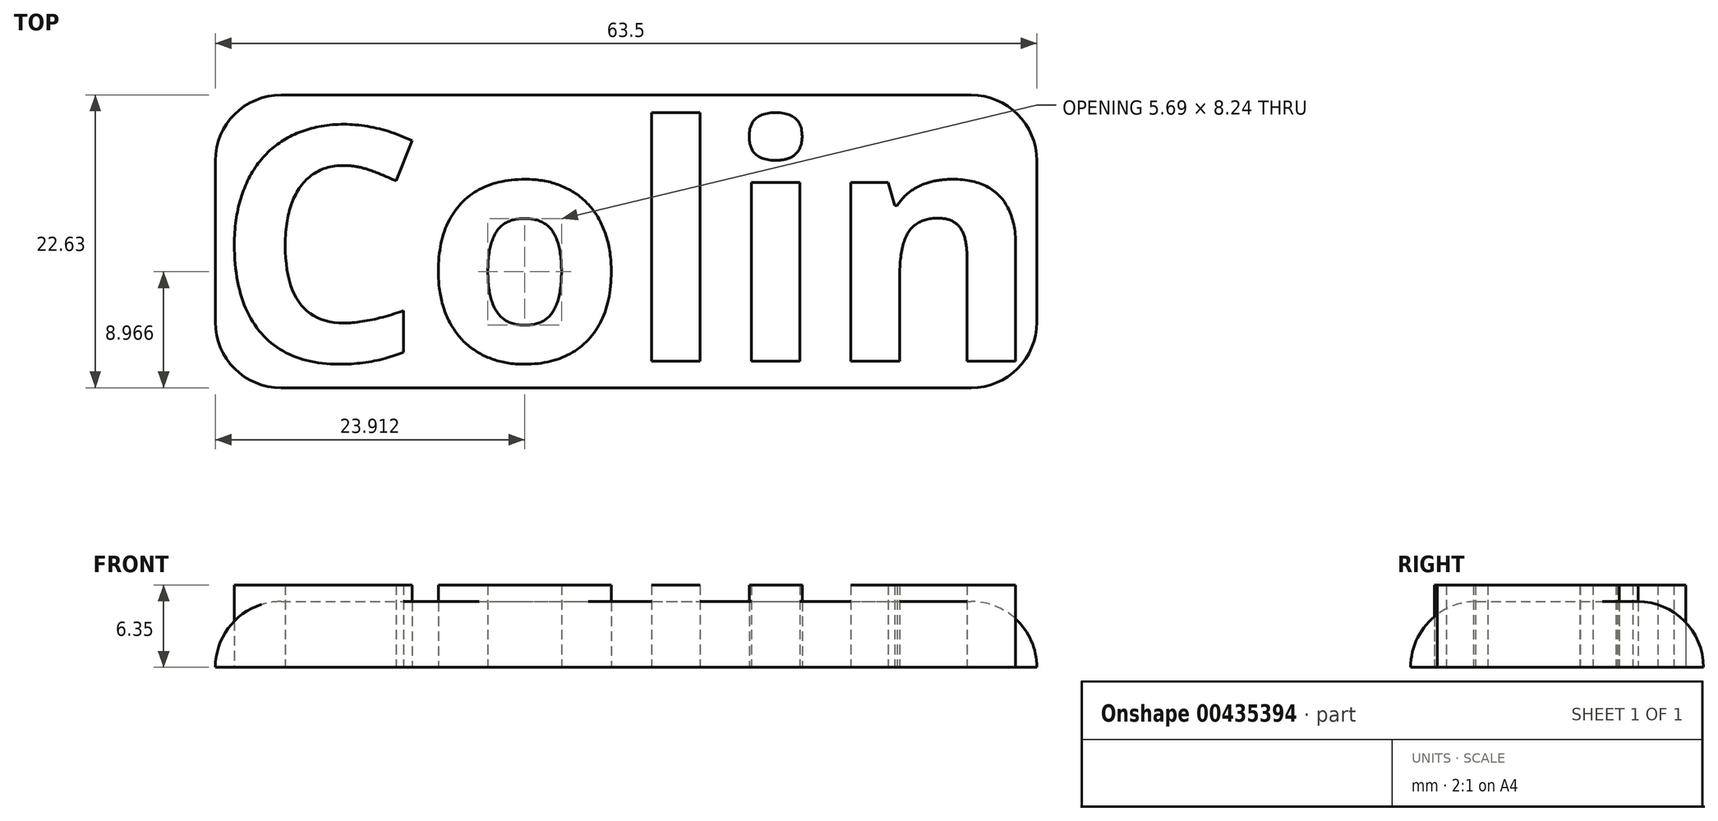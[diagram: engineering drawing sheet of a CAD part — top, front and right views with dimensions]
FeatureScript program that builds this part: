
annotation { "Feature Type Name" : "Feature", "Feature Type Description" : "" }
export const myFeature = defineFeature(function(context is Context, id is Id, definition is map)
    precondition{}
    {
        {
            var Q0;
            Q0=qCreatedBy(makeId("Top.planeOp"),FACE);
            var sketch = newSketch(context, id + "F0", { "sketchPlane" : qUnion([Q0])});
            skText(sketch, "E0", { "text": "Colin", "fontName": "OpenSans-Bold.ttf"});
            const initialGuessF0  = {"E0": [0, 0, 1, 0, 0.01819]};
            skSetInitialGuess(sketch, initialGuessF0);
            skSolve(sketch);
        }
        {
            var Q0;
            Q0=qCreatedBy(makeId("Top.planeOp"),FACE);
            var sketch = newSketch(context, id + "F1", { "sketchPlane" : qUnion([Q0])});
            skLineSegment(sketch, "E1.bottom", {"start": v(0, -2.07) * mm, "end": v(63.5, -2.07) * mm});
            skLineSegment(sketch, "E1.top", {"start": v(0, 20.56) * mm, "end": v(63.5, 20.56) * mm});
            skLineSegment(sketch, "E1.left", {"start": v(0, -2.07) * mm, "end": v(0, 20.56) * mm});
            skLineSegment(sketch, "E1.right", {"start": v(63.5, -2.07) * mm, "end": v(63.5, 20.56) * mm});
            skSolve(sketch);
        }
        {
            var Q0;
            Q0 = qSketchRegion(id + "F0", true);
            extrude(context, id + "F2", {"entities" : qUnion([Q0]), "depth" : 6.35 * mm});
        }
        {
            var Q0;
            Q0=makeQuery(id+"F1.imprint","IMPRINT",FACE,{"disambiguationData":[TD([[makeQuery(id+"F1.imprint","IMPRINT",EDGE,{"derivedFrom":sQuery(id+"F1.wireOp",EDGE,"E1.bottom")}),1.0]])]});
            extrude(context, id + "F3", {"entities" : qUnion([Q0]), "depth" : 5.08 * mm});
        }
        {
            var Q0;
            Q0=makeQuery(id+"F3.opExtrude","CAP_FACE",FACE,{"disambiguationData":[OSD([sQuery(id+"F1.wireOp",EDGE,"E1.bottom"),sQuery(id+"F1.wireOp",EDGE,"E1.top"),sQuery(id+"F1.wireOp",EDGE,"E1.left"),sQuery(id+"F1.wireOp",EDGE,"E1.right")])],"isStart":false});
            fillet(context, id + "F4", {"entities" : qUnion([Q0]), "radius" : 5.08 * mm, "tangentPropagation" : true, "allowEdgeOverflow" : false});
        }
        {
            var Q0;
            Q0=makeQuery(id+"F4.opFillet","BLEND_EDGE",EDGE,{"blendedFrom":[makeQuery(id+"F3.opExtrude","CAP_EDGE",EDGE,{"disambiguationData":[OSD([sQuery(id+"F1.wireOp",EDGE,"E1.top")])],"isStart":false}),makeQuery(id+"F3.opExtrude","CAP_EDGE",EDGE,{"disambiguationData":[OSD([sQuery(id+"F1.wireOp",EDGE,"E1.left")])],"isStart":false})],"blendedInto":[]});
            var Q1;
            Q1=makeQuery(id+"F4.opFillet","BLEND_EDGE",EDGE,{"blendedFrom":[makeQuery(id+"F3.opExtrude","CAP_EDGE",EDGE,{"disambiguationData":[OSD([sQuery(id+"F1.wireOp",EDGE,"E1.top")])],"isStart":false}),makeQuery(id+"F3.opExtrude","CAP_EDGE",EDGE,{"disambiguationData":[OSD([sQuery(id+"F1.wireOp",EDGE,"E1.right")])],"isStart":false})],"blendedInto":[]});
            var Q2;
            Q2=makeQuery(id+"F4.opFillet","BLEND_EDGE",EDGE,{"blendedFrom":[makeQuery(id+"F3.opExtrude","CAP_EDGE",EDGE,{"disambiguationData":[OSD([sQuery(id+"F1.wireOp",EDGE,"E1.bottom")])],"isStart":false}),makeQuery(id+"F3.opExtrude","CAP_EDGE",EDGE,{"disambiguationData":[OSD([sQuery(id+"F1.wireOp",EDGE,"E1.right")])],"isStart":false})],"blendedInto":[]});
            var Q3;
            Q3=makeQuery(id+"F4.opFillet","BLEND_EDGE",EDGE,{"blendedFrom":[makeQuery(id+"F3.opExtrude","CAP_EDGE",EDGE,{"disambiguationData":[OSD([sQuery(id+"F1.wireOp",EDGE,"E1.bottom")])],"isStart":false}),makeQuery(id+"F3.opExtrude","CAP_EDGE",EDGE,{"disambiguationData":[OSD([sQuery(id+"F1.wireOp",EDGE,"E1.left")])],"isStart":false})],"blendedInto":[]});
            fillet(context, id + "F5", {"entities" : qUnion([Q0, Q1, Q2, Q3]), "radius" : 5.08 * mm, "tangentPropagation" : true, "allowEdgeOverflow" : false});
        }
    });
